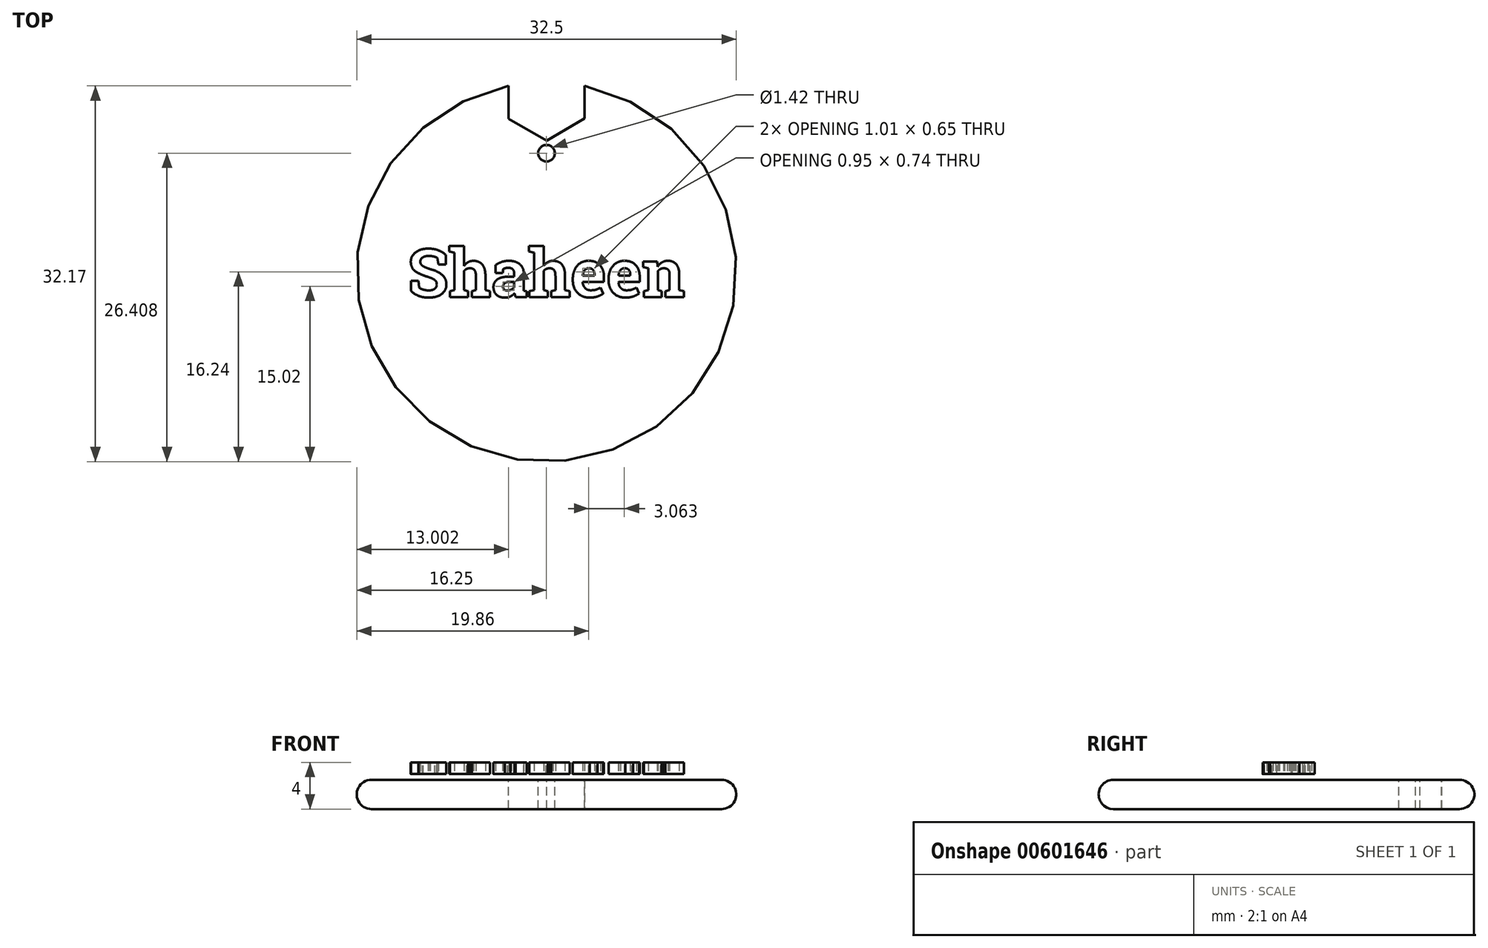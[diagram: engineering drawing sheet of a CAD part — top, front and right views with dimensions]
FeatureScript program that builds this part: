
annotation { "Feature Type Name" : "Feature", "Feature Type Description" : "" }
export const myFeature = defineFeature(function(context is Context, id is Id, definition is map)
    precondition{}
    {
        {
            var Q0;
            Q0=qCreatedBy(makeId("Front.planeOp"),FACE);
            var sketch = newSketch(context, id + "F0", { "sketchPlane" : qUnion([Q0])});
            skLineSegment(sketch, "E0.bottom", {"start": v(0, 0) * mm, "end": v(-15, 0) * mm});
            skLineSegment(sketch, "E0.top", {"start": v(0, 2.5) * mm, "end": v(-15, 2.5) * mm});
            skLineSegment(sketch, "E0.left", {"start": v(0, 0) * mm, "end": v(0, 2.5) * mm});
            skLineSegment(sketch, "E0.right", {"start": v(-15, 0) * mm, "end": v(-15, 2.5) * mm});
            skArc(sketch, "E1", {"start": v(-15, 2.5) * mm, "mid": v(-16.25, 1.25) * mm, "end": v(-15, 0) * mm});
            skSolve(sketch);
        }
        {
            var Q0;
            Q0 = qSketchRegion(id + "F0", true);
            var Q1;
            Q1=sQuery(id+"F0.wireOp",EDGE,"E0.left");
            revolve(context, id + "F1", {"entities" : qUnion([Q0]), "axis" : qUnion([Q1]), "revolveType" : RevolveType.FULL});
        }
        {
            var Q0;
            Q0=qCreatedBy(makeId("Top.planeOp"),FACE);
            cPlane(context, id + "F2", {"entities" : qUnion([Q0]), "cplaneType" : CPlaneType.OFFSET, "offset" : 3 * mm, "width" : 152.4 * mm, "height" : 152.4 * mm});
        }
        {
            var Q0;
            Q0=qCreatedBy(id+"F2.planeOp",FACE);
            var sketch = newSketch(context, id + "F3", { "sketchPlane" : qUnion([Q0])});
            skText(sketch, "E2", { "text": "Shaheen", "fontName": "RobotoSlab-Bold.ttf"});
            const initialGuessF3  = {"E2": [-0.01189, -0.00215, 1, 0, 0.00414]};
            skSetInitialGuess(sketch, initialGuessF3);
            skSolve(sketch);
        }
        {
            var Q0;
            Q0 = qSketchRegion(id + "F3", true);
            extrude(context, id + "F4", {"entities" : qUnion([Q0]), "depth" : 1 * mm, "offsetDistance" : 25.4 * mm});
        }
        {
            var Q0;
            Q0=makeQuery(id+"F1.opRevolve","SWEPT_FACE",FACE,{"disambiguationData":[OSD([sQuery(id+"F0.wireOp",EDGE,"E0.top")])]});
            var sketch = newSketch(context, id + "F5", { "sketchPlane" : qUnion([Q0])});
            skCircle(sketch, "E3.cCircle", {"center": v(0, 15) * mm, "radius": 3.25 * mm, "construction": true});
            skLineSegment(sketch, "E3.0", {"start": v(3.26, 13.13) * mm, "end": v(0.01, 11.25) * mm});
            skLineSegment(sketch, "E3.1", {"start": v(0.01, 11.25) * mm, "end": v(-3.24, 13.11) * mm});
            skLineSegment(sketch, "E3.2", {"start": v(-3.24, 13.11) * mm, "end": v(-3.26, 16.87) * mm});
            skLineSegment(sketch, "E3.3", {"start": v(-3.26, 16.87) * mm, "end": v(-0.01, 18.75) * mm});
            skLineSegment(sketch, "E3.4", {"start": v(-0.01, 18.75) * mm, "end": v(3.24, 16.89) * mm});
            skLineSegment(sketch, "E3.5", {"start": v(3.24, 16.89) * mm, "end": v(3.26, 13.13) * mm});
            skPoint(sketch, "E3.0.midPoint", {"position": v(1.63, 12.2) * mm});
            skSolve(sketch);
        }
        {
            var Q0;
            Q0 = qSketchRegion(id + "F5", true);
            extrude(context, id + "F6", {"entities" : qUnion([Q0]), "operationType" : NewBodyOperationType.REMOVE, "oppositeDirection" : true, "depth" : 25.4 * mm, "offsetDistance" : 25.4 * mm});
        }
        {
            var Q0;
            Q0=makeQuery(id+"F1.opRevolve","SWEPT_FACE",FACE,{"disambiguationData":[OSD([sQuery(id+"F0.wireOp",EDGE,"E0.top")])]});
            var sketch = newSketch(context, id + "F7", { "sketchPlane" : qUnion([Q0])});
            skCircle(sketch, "E4", {"center": v(0, 10.16) * mm, "radius": 0.71 * mm});
            skSolve(sketch);
        }
        {
            var Q0;
            Q0 = qSketchRegion(id + "F7", true);
            extrude(context, id + "F8", {"entities" : qUnion([Q0]), "operationType" : NewBodyOperationType.REMOVE, "oppositeDirection" : true, "depth" : 25.4 * mm, "offsetDistance" : 25.4 * mm});
        }
    });
